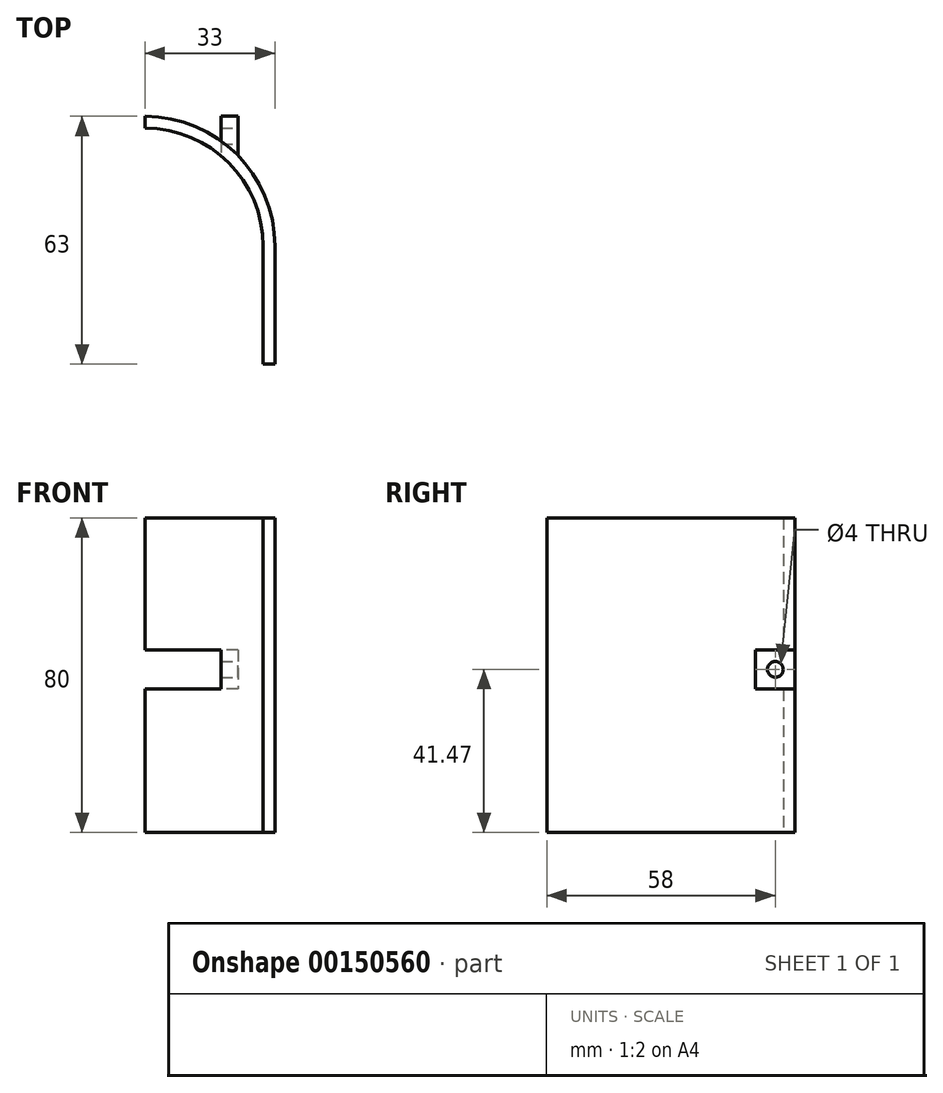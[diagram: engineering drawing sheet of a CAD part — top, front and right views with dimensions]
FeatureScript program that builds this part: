
annotation { "Feature Type Name" : "Feature", "Feature Type Description" : "" }
export const myFeature = defineFeature(function(context is Context, id is Id, definition is map)
    precondition{}
    {
        {
            var Q0;
            Q0=qCreatedBy(makeId("Top.planeOp"),FACE);
            var sketch = newSketch(context, id + "F0", { "sketchPlane" : qUnion([Q0])});
            skArc(sketch, "E0", {"start": v(30, 30) * mm, "mid": v(21.21, 51.21) * mm, "end": v(0, 60) * mm});
            skLineSegment(sketch, "E1", {"start": v(30, 30) * mm, "end": v(30, 0) * mm});
            skArc(sketch, "E2.0", {"start": v(33, 30) * mm, "mid": v(23.33, 53.33) * mm, "end": v(0, 63) * mm});
            skLineSegment(sketch, "E2.1", {"start": v(33, 30) * mm, "end": v(33, 0) * mm});
            skLineSegment(sketch, "E3", {"start": v(0, 63) * mm, "end": v(0, 60) * mm});
            skLineSegment(sketch, "E4", {"start": v(33, 0) * mm, "end": v(30, 0) * mm});
            skSolve(sketch);
        }
        {
            var Q0;
            Q0=makeQuery(id+"F0.imprint","IMPRINT",FACE,{"disambiguationData":[TD([[makeQuery(id+"F0.imprint","IMPRINT",EDGE,{"derivedFrom":sQuery(id+"F0.wireOp",EDGE,"E0")}),-1.0]])]});
            extrude(context, id + "F1", {"entities" : qUnion([Q0]), "depth" : 80 * mm});
        }
        {
            var Q0;
            Q0=qCreatedBy(makeId("Right.planeOp"),FACE);
            var sketch = newSketch(context, id + "F2", { "sketchPlane" : qUnion([Q0])});
            skLineSegment(sketch, "E5.bottom", {"start": v(53, 46.47) * mm, "end": v(63, 46.47) * mm});
            skLineSegment(sketch, "E5.top", {"start": v(53, 36.47) * mm, "end": v(63, 36.47) * mm});
            skLineSegment(sketch, "E5.left", {"start": v(53, 46.47) * mm, "end": v(53, 36.47) * mm});
            skLineSegment(sketch, "E5.right", {"start": v(63, 46.47) * mm, "end": v(63, 36.47) * mm});
            skSolve(sketch);
        }
        {
            var Q0;
            Q0=makeQuery(id+"F2.imprint","IMPRINT",FACE,{"disambiguationData":[TD([[makeQuery(id+"F2.imprint","IMPRINT",EDGE,{"derivedFrom":sQuery(id+"F2.wireOp",EDGE,"E5.bottom")}),-1.0]])]});
            extrude(context, id + "F3", {"entities" : qUnion([Q0]), "operationType" : NewBodyOperationType.REMOVE, "depth" : 62.75 * mm});
        }
        {
            var Q0;
            Q0=makeQuery(id+"F3.boolean.opBoolean","COPY",FACE,{"derivedFrom":makeQuery(id+"F3.opExtrude","SWEPT_FACE",FACE,{"disambiguationData":[OSD([sQuery(id+"F2.wireOp",EDGE,"E5.left")])]})});
            extrude(context, id + "F4", {"entities" : qUnion([Q0]), "operationType" : NewBodyOperationType.ADD, "depth" : 10 * mm});
        }
        {
            var Q0;
            Q0=makeQuery(id+"F4.opExtrude","SWEPT_FACE",FACE,{"disambiguationData":[OSD([sQuery(id+"F0.wireOp",EDGE,"E2.0"),sQuery(id+"F2.wireOp",EDGE,"E5.left")])]});
            var sketch = newSketch(context, id + "F5", { "sketchPlane" : qUnion([Q0])});
            skCircle(sketch, "E6", {"center": v(58, 41.47) * mm, "radius": 2 * mm});
            skPoint(sketch, "E6.centerSnap0", {"position": v(53, 41.47) * mm});
            skSolve(sketch);
        }
        {
            var Q0;
            Q0=makeQuery(id+"F5.imprint","IMPRINT",FACE,{"disambiguationData":[TD([[makeQuery(id+"F5.imprint","IMPRINT",EDGE,{"derivedFrom":sQuery(id+"F5.wireOp",EDGE,"E6")}),1.0]])]});
            extrude(context, id + "F6", {"entities" : qUnion([Q0]), "operationType" : NewBodyOperationType.REMOVE, "oppositeDirection" : true, "depth" : 25 * mm});
        }
    });
